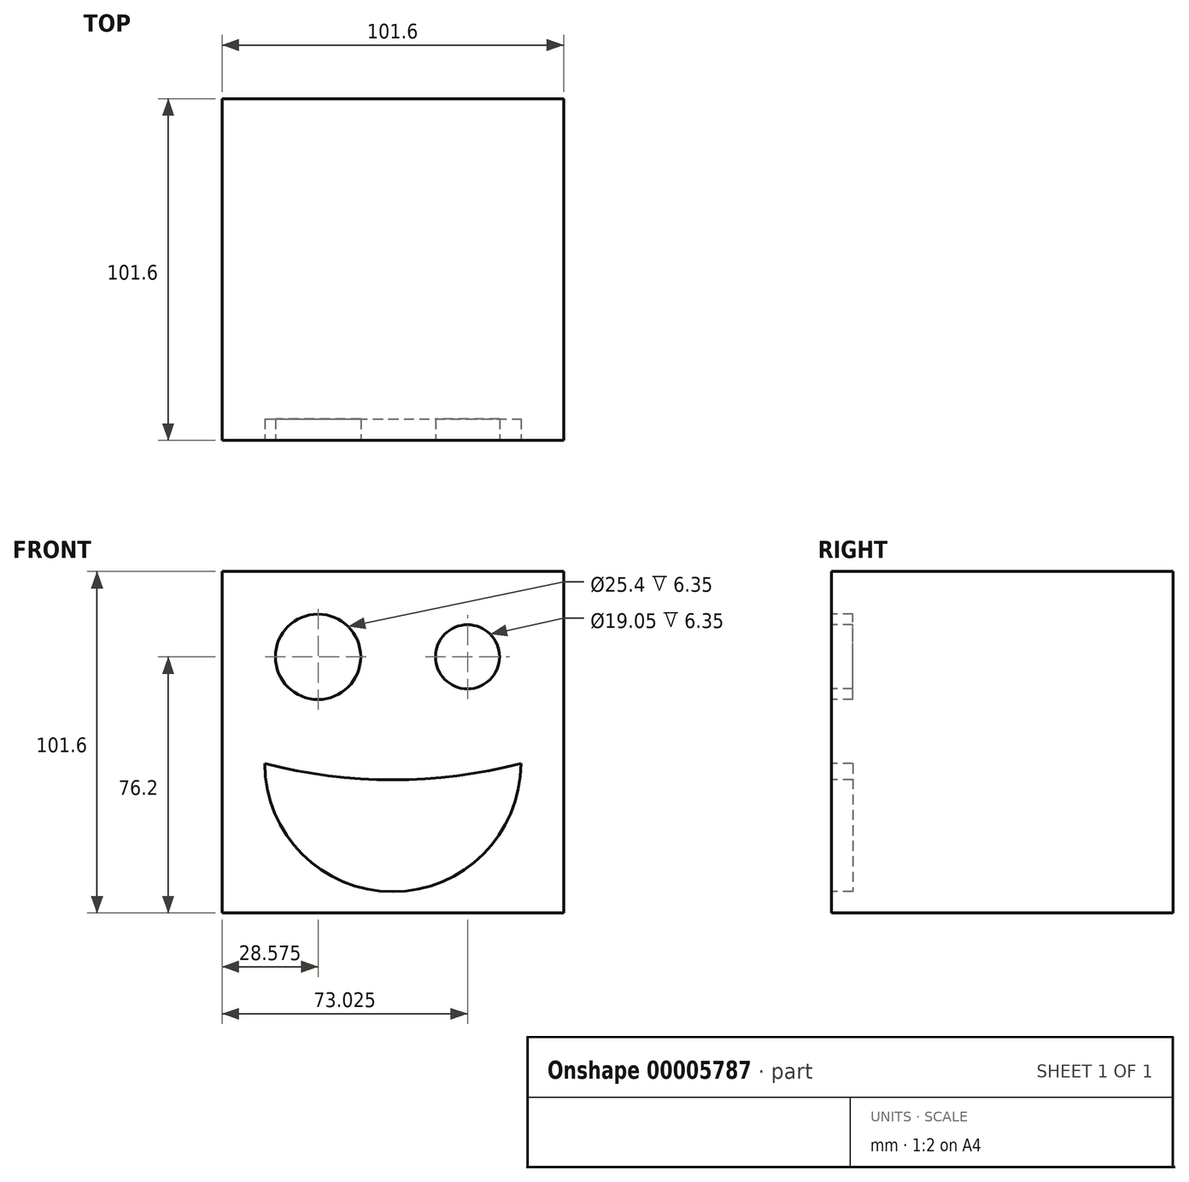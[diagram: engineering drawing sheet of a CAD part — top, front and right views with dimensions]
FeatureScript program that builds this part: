
annotation { "Feature Type Name" : "Feature", "Feature Type Description" : "" }
export const myFeature = defineFeature(function(context is Context, id is Id, definition is map)
    precondition{}
    {
        {
            var Q0;
            Q0=qCreatedBy(makeId("Top.planeOp"),FACE);
            var sketch = newSketch(context, id + "F0", { "sketchPlane" : qUnion([Q0])});
            skLineSegment(sketch, "E0.bottom", {"start": v(0, 0) * mm, "end": v(101.6, 0) * mm});
            skLineSegment(sketch, "E0.top", {"start": v(0, -101.6) * mm, "end": v(101.6, -101.6) * mm});
            skLineSegment(sketch, "E0.left", {"start": v(0, 0) * mm, "end": v(0, -101.6) * mm});
            skLineSegment(sketch, "E0.right", {"start": v(101.6, 0) * mm, "end": v(101.6, -101.6) * mm});
            skSolve(sketch);
        }
        {
            var Q0;
            Q0=makeQuery(id+"F0.imprint","IMPRINT",FACE,{"disambiguationData":[TD([[makeQuery(id+"F0.imprint","IMPRINT",EDGE,{"derivedFrom":sQuery(id+"F0.wireOp",EDGE,"E0.bottom")}),-1.0]])]});
            extrude(context, id + "F1", {"entities" : qUnion([Q0]), "depth" : 101.6 * mm});
        }
        {
            var Q0;
            Q0=makeQuery(id+"F1.opExtrude","SWEPT_FACE",FACE,{"disambiguationData":[OSD([sQuery(id+"F0.wireOp",EDGE,"E0.top")])]});
            var sketch = newSketch(context, id + "F2", { "sketchPlane" : qUnion([Q0])});
            skCircle(sketch, "E1", {"center": v(28.58, 76.2) * mm, "radius": 12.7 * mm});
            skCircle(sketch, "E2", {"center": v(73.03, 76.2) * mm, "radius": 9.53 * mm});
            skArc(sketch, "E3", {"start": v(12.7, 44.45) * mm, "mid": v(50.8, 6.35) * mm, "end": v(88.9, 44.45) * mm});
            skArc(sketch, "E4", {"start": v(12.7, 44.45) * mm, "mid": v(50.8, 39.61) * mm, "end": v(88.9, 44.45) * mm});
            skLineSegment(sketch, "E5", {"start": v(28.58, 76.2) * mm, "end": v(73.03, 76.2) * mm, "construction": true});
            skPoint(sketch, "E6", {"position": v(50.8, 76.2) * mm});
            skSolve(sketch);
        }
        {
            var Q0;
            Q0=makeQuery(id+"F2.imprint","IMPRINT",FACE,{"disambiguationData":[TD([[makeQuery(id+"F2.imprint","IMPRINT",EDGE,{"derivedFrom":sQuery(id+"F2.wireOp",EDGE,"E1")}),1.0]])]});
            var Q1;
            Q1=makeQuery(id+"F2.imprint","IMPRINT",FACE,{"disambiguationData":[TD([[makeQuery(id+"F2.imprint","IMPRINT",EDGE,{"derivedFrom":sQuery(id+"F2.wireOp",EDGE,"E2")}),1.0]])]});
            var Q2;
            Q2=makeQuery(id+"F2.imprint","IMPRINT",FACE,{"disambiguationData":[TD([[makeQuery(id+"F2.imprint","IMPRINT",EDGE,{"derivedFrom":sQuery(id+"F2.wireOp",EDGE,"E3")}),1.0]])]});
            extrude(context, id + "F3", {"entities" : qUnion([Q0, Q1, Q2]), "operationType" : NewBodyOperationType.REMOVE, "oppositeDirection" : true, "depth" : 6.35 * mm});
        }
    });
